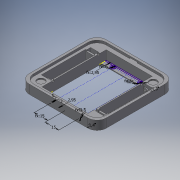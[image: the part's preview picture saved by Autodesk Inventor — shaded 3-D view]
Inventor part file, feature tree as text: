
AUTODESK INVENTOR PART (.ipt)
format: ipt  version: 2016 SP2 (Build 200236200, 236)  size: 416,256 bytes
history: native  units: mm
features: sketch x11, extrude x10, fillet x1, chamfer x1
ambient origin geometry x8: Origin, YZ Plane, XZ Plane, XY Plane, X Axis, Y Axis, Z Axis, Center Point
bodies: Volumenkörper1 (feature_tree)
feature tree (23):
  extrude  "Extrusion1"  Depth=70.3mm
  extrude  "Extrusion2"  Depth=5.0mm
  extrude  "Extrusion7"  Depth=10.5mm
  extrude  "Extrusion8"  Depth=48.3mm
  extrude  "Extrusion9"  Depth=1.2mm
  extrude  "Extrusion10"  Depth=0.8mm
  extrude  "Extrusion12"  Depth=3.0mm
  extrude  "Extrusion13"  Depth=2.0mm
  extrude  "Extrusion14"  Depth=0.5mm
  extrude  "Extrusion15"  Depth=0.8mm
  fillet  "Rundung1"  Radius=0.5mm
  chamfer  "Fase3"  Distance=3.75mm
  sketch  "Skizze17"  dims[d23=3.0mm d26=3.75mm d27=2.0mm d28=0.5mm d30=3.0mm d31=0.8mm d32=0.8mm d33=1.6mm d34=1.0mm d35=1.0mm d36=3.0mm d37=3.0mm d38=1.0mm d39=1.0mm d40=1.6mm d41=10.0mm d42=0.0mm d44=59.0mm d45=2.0mm d46=0.8mm d47=0.0mm d80=8.15mm d81=8.15mm d82=6.0mm d83=6.0mm d84=6.0mm d85=6.0mm d86=1.4mm d87=0.0mm d88=3.0mm d89=3.0mm d90=3.8mm d91=0.0mm d92=3.0mm d93=3.0mm d94=3.8mm d95=0.0mm d96=8.5mm d97=0.5mm d98=0.5mm d99=2.0mm d100=0.5mm d101=2.0mm d102=0.5mm d103=1.6mm d104=8.5mm d105=2.0mm d106=0.5mm d107=1.5mm d108=0.0mm d122=2.6mm d123=0.0mm d124=1.9mm d125=0.6mm d126=5.2mm d127=1.0mm d128=5.2mm d129=1.0mm d130=1.2mm d131=0.0mm d132=4.1mm d133=1.0mm d134=8.2mm d135=1.2mm d136=0.0mm d137=10.8mm d138=0.0mm d139=10.0mm d140=5.3mm d141=1.2mm d142=6.108652mm d147=29.5mm d150=1.4mm d151=1.3mm d152=5.0mm d153=3.0mm d154=3.0mm d155=5.0mm d156=3.0mm d157=5.0mm d158=3.0mm d159=5.0mm d160=2.95mm d161=2.95mm d162=15.0mm d163=15.0mm]
  sketch  "Skizze1"  dims[d0=50.3mm d1=70.3mm]
  sketch  "Skizze2"  dims[d2=5.0mm d3=5.0mm]
  sketch  "Skizze7"  dims[d4=10.5mm d5=10.5mm]
  sketch  "Skizze8"  dims[d6=48.3mm d7=48.3mm]
  sketch  "Skizze9"  dims[d8=1.2mm d9=1.2mm]
  sketch  "Skizze10"  dims[d11=0.8mm d12=0.8mm]
  sketch  "Skizze12"  dims[d13=0.8mm d14=3.0mm]
  sketch  "Skizze13"  dims[d15=3.75mm d16=2.0mm]
  sketch  "Skizze14"  dims[d17=3.0mm d18=0.5mm]
  sketch  "Skizze15"  dims[d19=0.5mm d20=0.8mm d21=0.5mm d22=0.5mm]
